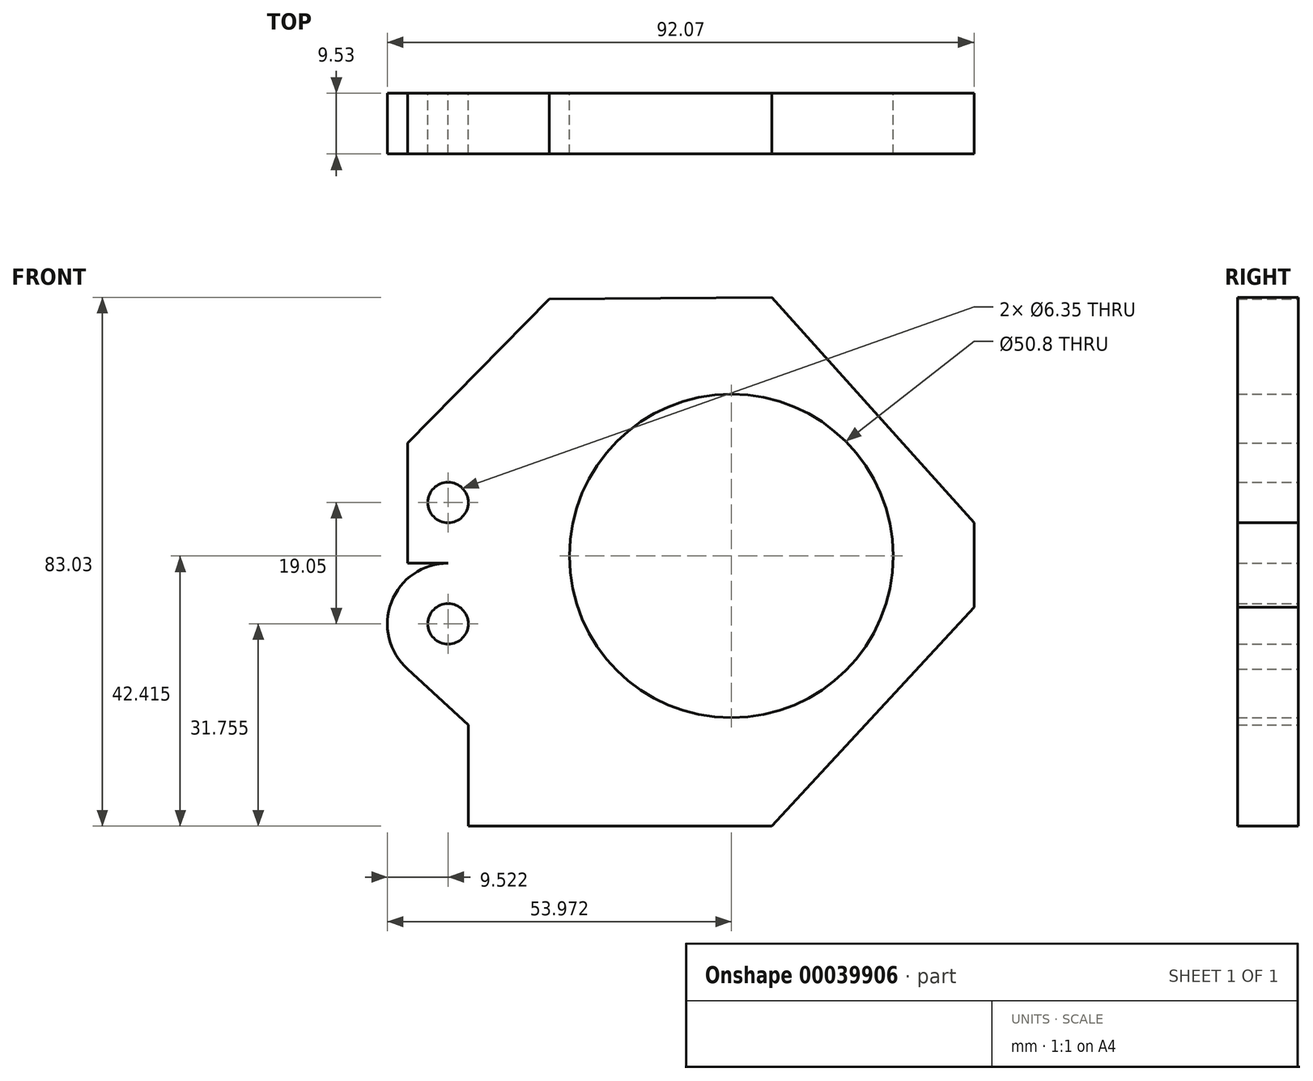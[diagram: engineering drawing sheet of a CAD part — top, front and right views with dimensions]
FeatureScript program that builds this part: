
annotation { "Feature Type Name" : "Feature", "Feature Type Description" : "" }
export const myFeature = defineFeature(function(context is Context, id is Id, definition is map)
    precondition{}
    {
        {
            var Q0;
            Q0=qCreatedBy(makeId("Front.planeOp"),FACE);
            var sketch = newSketch(context, id + "F0", { "sketchPlane" : qUnion([Q0])});
            skLineSegment(sketch, "E0", {"start": v(-46.04, 12.51) * mm, "end": v(-46.04, -6.35) * mm});
            skLineSegment(sketch, "E1", {"start": v(-36.51, -47.63) * mm, "end": v(11.11, -47.62) * mm});
            skCircle(sketch, "E2", {"center": v(4.76, -5.21) * mm, "radius": 25.4 * mm});
            skLineSegment(sketch, "E3", {"start": v(42.86, -13.26) * mm, "end": v(42.86, 0) * mm});
            skLineSegment(sketch, "E4", {"start": v(11.11, 35.4) * mm, "end": v(-23.81, 35.1) * mm});
            skLineSegment(sketch, "E5", {"start": v(-46.04, -6.35) * mm, "end": v(42.86, -6.35) * mm});
            skLineSegment(sketch, "E6", {"start": v(11.11, 35.4) * mm, "end": v(42.86, 0) * mm});
            skLineSegment(sketch, "E7", {"start": v(42.86, -13.26) * mm, "end": v(11.11, -47.63) * mm});
            skLineSegment(sketch, "E8", {"start": v(-23.81, 35.1) * mm, "end": v(-46.04, 12.51) * mm});
            skCircle(sketch, "E9", {"center": v(-39.69, 3.17) * mm, "radius": 3.18 * mm});
            skCircle(sketch, "E10.MirrorC", {"center": v(-39.69, -15.87) * mm, "radius": 3.18 * mm});
            skLineSegment(sketch, "E11", {"start": v(-36.51, -47.63) * mm, "end": v(-36.51, -31.75) * mm});
            skArc(sketch, "E12", {"start": v(-39.69, -6.35) * mm, "mid": v(-48.59, -12.48) * mm, "end": v(-46.04, -22.97) * mm});
            skLineSegment(sketch, "E13", {"start": v(-36.51, -31.75) * mm, "end": v(-46.04, -22.97) * mm});
            skPoint(sketch, "E14.orphan", {"position": v(-46.04, 34.93) * mm});
            skPoint(sketch, "E15.orphan", {"position": v(42.86, 35.66) * mm});
            skPoint(sketch, "E16.orphan", {"position": v(42.86, -47.62) * mm});
            skPoint(sketch, "E17.orphan", {"position": v(-46.04, -47.63) * mm});
            skSolve(sketch);
        }
        {
            var Q0;
            {var subQ5=sQuery(id+"F0.wireOp",EDGE,"E0");Q0=makeQuery(id+"F0.imprint","IMPRINT",FACE,{"disambiguationData":[TD([[makeQuery(id+"F0.imprint","IMPRINT",EDGE,{"derivedFrom":subQ5}),1.0]])]});}
            extrude(context, id + "F1", {"entities" : qUnion([Q0]), "depth" : 9.52 * mm});
        }
        {
            var Q0;
            Q0=makeQuery(id+"F0.imprint","IMPRINT",FACE,{"disambiguationData":[TD([[makeQuery(id+"F0.imprint","IMPRINT",EDGE,{"derivedFrom":sQuery(id+"F0.wireOp",EDGE,"E1")}),1.0]])]});
            extrude(context, id + "F2", {"entities" : qUnion([Q0]), "operationType" : NewBodyOperationType.ADD, "depth" : 9.52 * mm});
        }
    });
